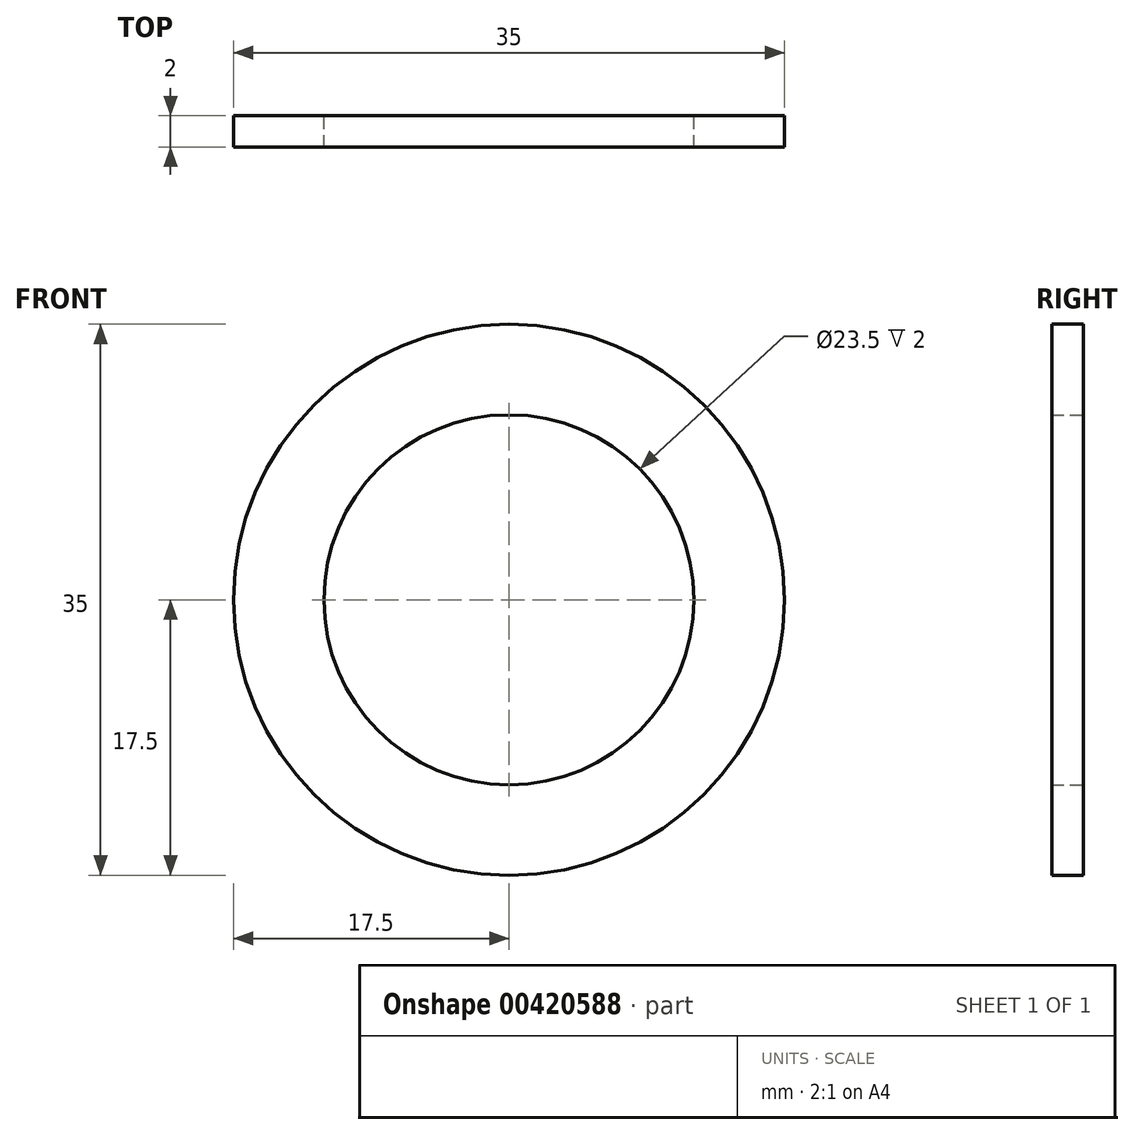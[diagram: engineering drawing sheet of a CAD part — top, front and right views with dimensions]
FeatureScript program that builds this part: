
annotation { "Feature Type Name" : "Feature", "Feature Type Description" : "" }
export const myFeature = defineFeature(function(context is Context, id is Id, definition is map)
    precondition{}
    {
        {
            var Q0;
            Q0=qCreatedBy(makeId("Front.planeOp"),FACE);
            var sketch = newSketch(context, id + "F0", { "sketchPlane" : qUnion([Q0])});
            skCircle(sketch, "E0", {"center": v(0, 0) * mm, "radius": 17.5 * mm});
            skCircle(sketch, "E1", {"center": v(0, 0) * mm, "radius": 11.75 * mm});
            skSolve(sketch);
        }
        {
            var Q0;
            Q0 = qSketchRegion(id + "F0", true);
            extrude(context, id + "F1", {"entities" : qUnion([Q0]), "depth" : 2 * mm, "offsetDistance" : 25 * mm, "symmetric" : true});
        }
    });
